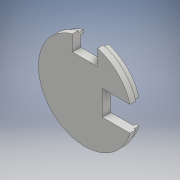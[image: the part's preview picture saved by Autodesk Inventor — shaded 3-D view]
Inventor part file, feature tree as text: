
AUTODESK INVENTOR PART (.ipt)
format: ipt  version: 2018 (Build 220112000, 112)  size: 248,832 bytes
history: native  units: mm
features: extrude x8, sketch x8, fillet x2, pattern_circular x1
ambient origin geometry x8: Origin, YZ Plane, XZ Plane, XY Plane, X Axis, Y Axis, Z Axis, Center Point
bodies: Solid1 (feature_tree)
feature tree (19):
  extrude  "Extrusion1"  Depth=30.0mm
  extrude  "Extrusion4"  TaperAngle=45.0deg  [1 undecoded]
  extrude  "Extrusion3"  Depth=15.0mm
  fillet  "Fillet1"  [1 undecoded]
  extrude  "Extrusion5"  Depth=3.0mm
  extrude  "Extrusion6"  Depth=15.0mm
  extrude  "Extrusion7"  Depth=15.0mm
  fillet  "Fillet2"  [1 undecoded]
  pattern_circular  "Circular Pattern1"  [2 undecoded]
  extrude  "Extrusion8"  Depth=1.0mm
  extrude  "Extrusion9"  Depth=3.5mm
  sketch  "Sketch1"  dims[d0=50.0mm d1=30.0mm]
  sketch  "Sketch3"  dims[d2=15.0mm d3=45.0deg]
  sketch  "Sketch6"  dims[d4=3.0mm d5=15.0mm d6=135.0deg]
  sketch  "Sketch7"  dims[d7=3.0mm d8=54.0mm]
  sketch  "Sketch8"  dims[d9=6.5mm d10=0.0mm d21=15.0mm]
  sketch  "Sketch9"  dims[d22=135.0deg d23=15.0mm d24=45.0deg]
  sketch  "Sketch10"  dims[d25=2.8mm]
  sketch  "Sketch11"  dims[d26=2.8mm d27=2.0mm d28=0.0mm d29=1.0mm d30=50.5mm d31=1.5mm d32=0.0mm d33=27.0mm d34=6.108652mm d35=3.490659mm d36=26.0mm d37=6.108652mm d38=3.490659mm d39=3.0mm d40=0.0mm d41=27.0mm d42=6.981317mm d43=15.0deg d44=26.0mm d45=6.981317mm d46=15.0deg d47=1.5mm d48=0.0mm d49=27.0mm d50=8.901179mm d51=0.174533mm d52=26.0mm d53=8.901179mm d54=0.174533mm d55=0.1mm d56=0.0mm d57=0.3mm d58=20.0mm d59=360.0deg d61=56.0mm d62=3.5mm d63=0.0mm d68=17.5mm d69=7.5mm d70=17.5mm d71=7.5mm d72=0.0mm d73=0.0mm d74=7.5mm d75=10.5mm d76=7.5mm d77=10.5mm]
note: 5 required parameter values undecoded (feature->parameter linkage not recoverable at this tier; creation-order binding heuristic only, values carry confidence <= 0.55)
